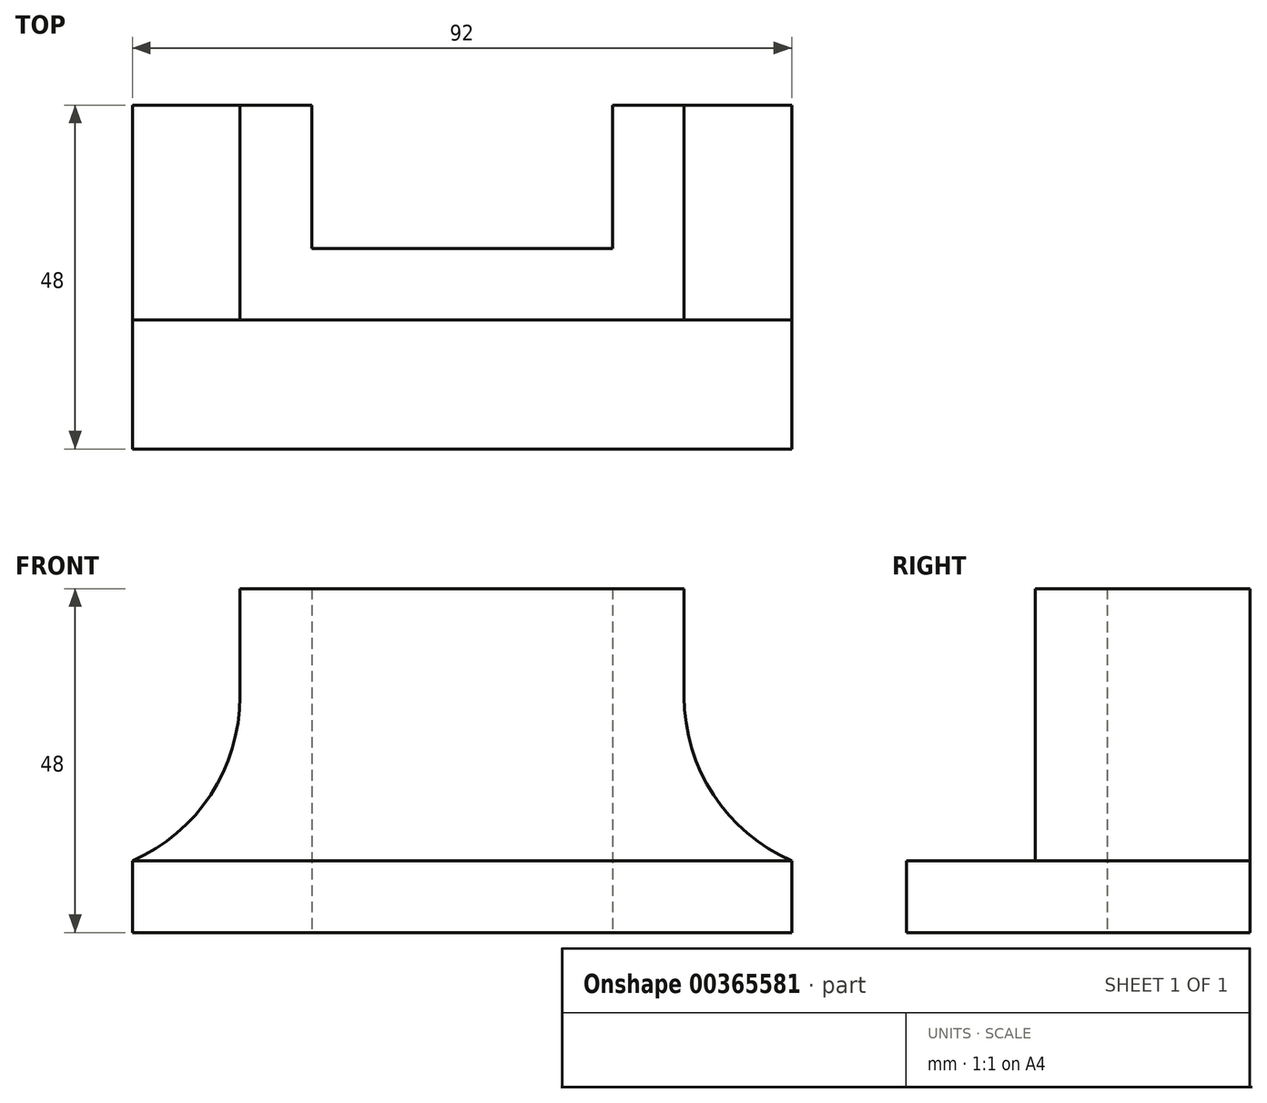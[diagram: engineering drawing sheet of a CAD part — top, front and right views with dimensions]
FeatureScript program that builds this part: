
annotation { "Feature Type Name" : "Feature", "Feature Type Description" : "" }
export const myFeature = defineFeature(function(context is Context, id is Id, definition is map)
    precondition{}
    {
        {
            var Q0;
            Q0=qCreatedBy(makeId("Top.planeOp"),FACE);
            var sketch = newSketch(context, id + "F0", { "sketchPlane" : qUnion([Q0])});
            skLineSegment(sketch, "E0", {"start": v(0, 0) * mm, "end": v(21, 0) * mm});
            skLineSegment(sketch, "E1", {"start": v(21, 0) * mm, "end": v(21, 20) * mm});
            skLineSegment(sketch, "E2", {"start": v(21, 20) * mm, "end": v(46, 20) * mm});
            skLineSegment(sketch, "E3", {"start": v(46, 20) * mm, "end": v(46, -28) * mm});
            skLineSegment(sketch, "E4", {"start": v(46, -28) * mm, "end": v(-46, -28) * mm});
            skLineSegment(sketch, "E5", {"start": v(-46, -28) * mm, "end": v(-46, 20) * mm});
            skLineSegment(sketch, "E6", {"start": v(-46, 20) * mm, "end": v(-21, 20) * mm});
            skLineSegment(sketch, "E7", {"start": v(-21, 20) * mm, "end": v(-21, 0) * mm});
            skLineSegment(sketch, "E8", {"start": v(-21, 0) * mm, "end": v(0, 0) * mm});
            skLineSegment(sketch, "E9", {"start": v(-46, -10) * mm, "end": v(46, -10) * mm});
            skLineSegment(sketch, "E10", {"start": v(-31, 20) * mm, "end": v(-31, -10) * mm});
            skLineSegment(sketch, "E11", {"start": v(31, 20) * mm, "end": v(31, -10) * mm});
            skSolve(sketch);
        }
        {
            var Q0;
            Q0=makeQuery(id+"F0.imprint","IMPRINT",FACE,{"disambiguationData":[TD([[makeQuery(id+"F0.imprint","IMPRINT",EDGE,{"derivedFrom":sQuery(id+"F0.wireOp",EDGE,"E0")}),-1.0]])]});
            var Q1;
            {var subQ3=sQuery(id+"F0.wireOp",EDGE,"E11");Q1=makeQuery(id+"F0.imprint","IMPRINT",FACE,{"disambiguationData":[TD([[makeQuery(id+"F0.imprint","IMPRINT",EDGE,{"derivedFrom":subQ3}),1.0]])]});}
            var Q2;
            {var subQ5=sQuery(id+"F0.wireOp",EDGE,"E10");Q2=makeQuery(id+"F0.imprint","IMPRINT",FACE,{"disambiguationData":[TD([[makeQuery(id+"F0.imprint","IMPRINT",EDGE,{"derivedFrom":subQ5}),-1.0]])]});}
            extrude(context, id + "F1", {"entities" : qUnion([Q0, Q1, Q2]), "depth" : 48 * mm});
        }
        {
            var Q0;
            {var subQ4=sQuery(id+"F0.wireOp",EDGE,"E4");Q0=makeQuery(id+"F0.imprint","IMPRINT",FACE,{"disambiguationData":[TD([[makeQuery(id+"F0.imprint","IMPRINT",EDGE,{"derivedFrom":subQ4}),-1.0]])]});}
            extrude(context, id + "F2", {"entities" : qUnion([Q0]), "operationType" : NewBodyOperationType.ADD, "depth" : 10 * mm});
        }
        {
            var Q0;
            Q0=makeQuery(id+"F1.opExtrude","CAP_FACE",FACE,{"disambiguationData":[OSD([sQuery(id+"F0.wireOp",EDGE,"E0"),sQuery(id+"F0.wireOp",EDGE,"E1"),sQuery(id+"F0.wireOp",EDGE,"E2"),sQuery(id+"F0.wireOp",EDGE,"E3"),sQuery(id+"F0.wireOp",EDGE,"E5"),sQuery(id+"F0.wireOp",EDGE,"E6"),sQuery(id+"F0.wireOp",EDGE,"E7"),sQuery(id+"F0.wireOp",EDGE,"E8"),sQuery(id+"F0.wireOp",EDGE,"E9")])],"isStart":false});
            var sketch = newSketch(context, id + "F3", { "sketchPlane" : qUnion([Q0])});
            skLineSegment(sketch, "E12", {"start": v(31, 20) * mm, "end": v(21, 20) * mm});
            skLineSegment(sketch, "E13", {"start": v(21, 20) * mm, "end": v(21, -10) * mm});
            skLineSegment(sketch, "E14", {"start": v(21, -10) * mm, "end": v(31, -10) * mm});
            skLineSegment(sketch, "E15", {"start": v(31, -10) * mm, "end": v(31, 20) * mm});
            skLineSegment(sketch, "E16.MirrorCS", {"start": v(-31, 20) * mm, "end": v(-21, 20) * mm});
            skLineSegment(sketch, "E17.MirrorCS", {"start": v(-21, 20) * mm, "end": v(-21, -10) * mm});
            skLineSegment(sketch, "E18.MirrorCS", {"start": v(-21, -10) * mm, "end": v(-31, -10) * mm});
            skLineSegment(sketch, "E19.MirrorCS", {"start": v(-31, -10) * mm, "end": v(-31, 20) * mm});
            skSolve(sketch);
        }
        {
            var Q0;
            {var subQ0=sQuery(id+"F3.wireOp",EDGE,"E19.MirrorCS");Q0=makeQuery(id+"F3.imprint","IMPRINT",FACE,{"disambiguationData":[TD([[makeQuery(id+"F3.imprint","IMPRINT",EDGE,{"derivedFrom":subQ0}),1.0]])]});}
            var Q1;
            {var subQ0=sQuery(id+"F3.wireOp",EDGE,"E15");Q1=makeQuery(id+"F3.imprint","IMPRINT",FACE,{"disambiguationData":[TD([[makeQuery(id+"F3.imprint","IMPRINT",EDGE,{"derivedFrom":subQ0}),-1.0]])]});}
            extrude(context, id + "F4", {"entities" : qUnion([Q0, Q1]), "operationType" : NewBodyOperationType.REMOVE, "oppositeDirection" : true, "depth" : 38 * mm});
        }
        {
            var Q0;
            Q0=makeQuery(id+"F4.boolean.opBoolean","COPY",EDGE,{"derivedFrom":makeQuery(id+"F4.opExtrude","CAP_EDGE",EDGE,{"disambiguationData":[OSD([sQuery(id+"F3.wireOp",EDGE,"E15")])],"isStart":false})});
            var Q1;
            Q1=makeQuery(id+"F4.boolean.opBoolean","COPY",EDGE,{"derivedFrom":makeQuery(id+"F4.opExtrude","CAP_EDGE",EDGE,{"disambiguationData":[OSD([sQuery(id+"F3.wireOp",EDGE,"E19.MirrorCS")])],"isStart":false})});
            fillet(context, id + "F5", {"entities" : qUnion([Q0, Q1]), "radius" : 25 * mm, "tangentPropagation" : true, "allowEdgeOverflow" : false});
        }
    });
